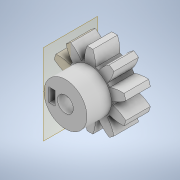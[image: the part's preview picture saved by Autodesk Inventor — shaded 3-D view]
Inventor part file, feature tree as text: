
AUTODESK INVENTOR PART (.ipt)
format: ipt  version: 2020 (Build 240168000, 168)  size: 212,992 bytes
history: native  units: in
note: dims shown in document units (in); Inventor stores cm internally (conversion verified against a paired STEP export)
features: extrude x5, sketch x5, other x2, plane x1
ambient origin geometry x8: Origin, YZ Plane, XZ Plane, XY Plane, X Axis, Y Axis, Z Axis, Center Point
bodies: Solid1 (feature_tree)
feature tree (13):
  extrude  "Extrusion1"  Depth=0.3937in
  other  "Spur Gear Teeth1"
  extrude  "Extrusion2"  Depth=0.3937in TaperAngle=0.0deg
  extrude  "Extrusion3"  Depth=0.3937in TaperAngle=0.0deg
  plane  "Work Plane1"
  extrude  "Extrusion5"  Depth=0.1181in
  extrude  "Extrusion6"  Depth=0.3937in TaperAngle=0.0deg
  sketch  "Sketch1"  dims[d0=0.3937in d1=0.0in d2=1.9685in]
  other  "Spur Gear1"
  sketch  "Sketch2"  dims[d3=0.689in d4=0.3937in d5=0.0in]
  sketch  "Sketch3"  dims[d6=0.2539in d7=0.3937in d8=0.0in]
  sketch  "Sketch5"  dims[d11=-0.3125in d12=0.1181in]
  sketch  "Sketch6"  dims[d13=0.5906in d14=0.3937in d15=0.0in d17=0.0984in d19=0.1083in d20=0.2165in d21=0.2953in d22=0.0in d23=0.2165in]
